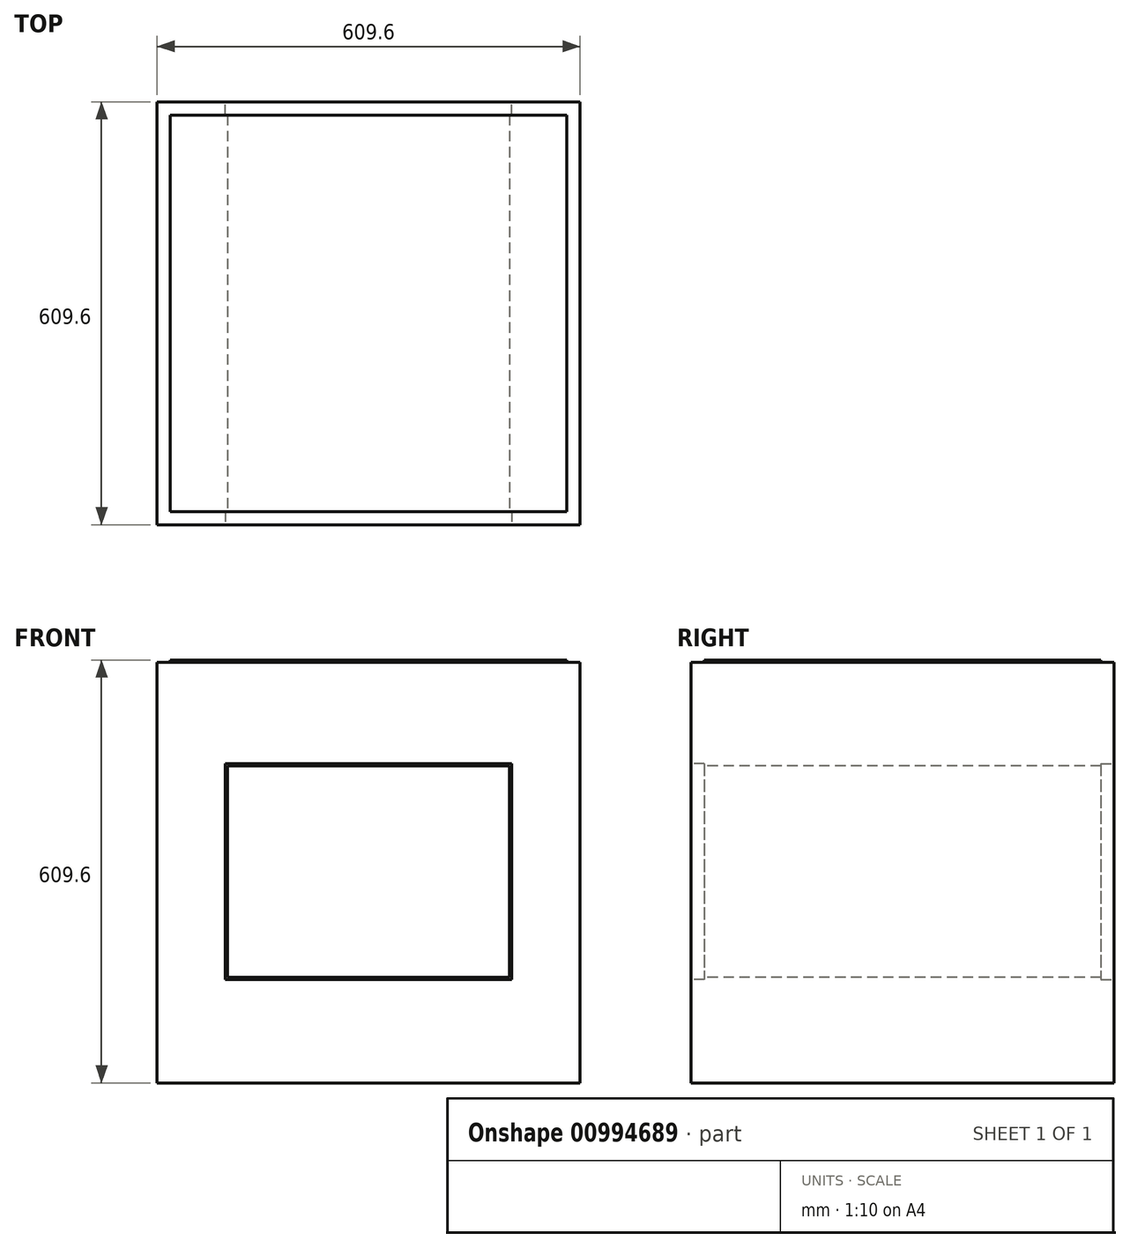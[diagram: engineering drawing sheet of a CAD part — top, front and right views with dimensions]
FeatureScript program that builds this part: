
annotation { "Feature Type Name" : "Feature", "Feature Type Description" : "" }
export const myFeature = defineFeature(function(context is Context, id is Id, definition is map)
    precondition{}
    {
        {
            var Q0;
            Q0=qCreatedBy(makeId("Front.planeOp"),FACE);
            var sketch = newSketch(context, id + "F0", { "sketchPlane" : qUnion([Q0])});
            skLineSegment(sketch, "E0.bottom", {"start": v(0, 0) * mm, "end": v(-609.6, 0) * mm});
            skLineSegment(sketch, "E0.top", {"start": v(0, 609.6) * mm, "end": v(-609.6, 609.6) * mm});
            skLineSegment(sketch, "E0.left", {"start": v(0, 0) * mm, "end": v(0, 609.6) * mm});
            skLineSegment(sketch, "E0.right", {"start": v(-609.6, 0) * mm, "end": v(-609.6, 609.6) * mm});
            skLineSegment(sketch, "E1.bottom", {"start": v(-508, 457.2) * mm, "end": v(-101.6, 457.2) * mm});
            skLineSegment(sketch, "E1.top", {"start": v(-508, 152.4) * mm, "end": v(-101.6, 152.4) * mm});
            skLineSegment(sketch, "E1.left", {"start": v(-508, 457.2) * mm, "end": v(-508, 152.4) * mm});
            skLineSegment(sketch, "E1.right", {"start": v(-101.6, 457.2) * mm, "end": v(-101.6, 152.4) * mm});
            skSolve(sketch);
        }
        {
            var Q0;
            Q0 = qSketchRegion(id + "F0", true);
            extrude(context, id + "F1", {"entities" : qUnion([Q0]), "oppositeDirection" : true, "depth" : 609.6 * mm, "offsetDistance" : 25.4 * mm});
        }
        {
            var Q0;
            Q0=makeQuery(id+"F1.opExtrude","SWEPT_FACE",FACE,{"disambiguationData":[OSD([sQuery(id+"F0.wireOp",EDGE,"E0.top")])]});
            var sketch = newSketch(context, id + "F2", { "sketchPlane" : qUnion([Q0])});
            skLineSegment(sketch, "E2.0", {"start": v(-590.55, 19.05) * mm, "end": v(-19.05, 19.05) * mm});
            skLineSegment(sketch, "E2.1", {"start": v(-590.55, 590.55) * mm, "end": v(-590.55, 19.05) * mm});
            skLineSegment(sketch, "E2.2", {"start": v(-19.05, 590.55) * mm, "end": v(-590.55, 590.55) * mm});
            skLineSegment(sketch, "E2.3", {"start": v(-19.05, 19.05) * mm, "end": v(-19.05, 590.55) * mm});
            skLineSegment(sketch, "E3.bottom", {"start": v(-609.6, 0) * mm, "end": v(0, 0) * mm});
            skLineSegment(sketch, "E3.top", {"start": v(-609.6, 609.6) * mm, "end": v(0, 609.6) * mm});
            skLineSegment(sketch, "E3.left", {"start": v(-609.6, 0) * mm, "end": v(-609.6, 609.6) * mm});
            skLineSegment(sketch, "E3.right", {"start": v(0, 0) * mm, "end": v(0, 609.6) * mm});
            skSolve(sketch);
        }
        {
            var Q0;
            Q0 = qSketchRegion(id + "F2", true);
            extrude(context, id + "F3", {"entities" : qUnion([Q0]), "operationType" : NewBodyOperationType.REMOVE, "oppositeDirection" : true, "depth" : 3.17 * mm, "offsetDistance" : 25.4 * mm});
        }
        {
            var Q0;
            Q0=makeQuery(id+"F1.opExtrude","CAP_FACE",FACE,{"disambiguationData":[OSD([sQuery(id+"F0.wireOp",EDGE,"E0.bottom"),sQuery(id+"F0.wireOp",EDGE,"E0.top"),sQuery(id+"F0.wireOp",EDGE,"E0.left"),sQuery(id+"F0.wireOp",EDGE,"E0.right"),sQuery(id+"F0.wireOp",EDGE,"E1.bottom"),sQuery(id+"F0.wireOp",EDGE,"E1.top"),sQuery(id+"F0.wireOp",EDGE,"E1.left"),sQuery(id+"F0.wireOp",EDGE,"E1.right")])],"isStart":true});
            var sketch = newSketch(context, id + "F4", { "sketchPlane" : qUnion([Q0])});
            skLineSegment(sketch, "E4.bottom", {"start": v(-511.18, 460.37) * mm, "end": v(-98.43, 460.37) * mm});
            skLineSegment(sketch, "E4.top", {"start": v(-511.18, 149.22) * mm, "end": v(-98.43, 149.22) * mm});
            skLineSegment(sketch, "E4.left", {"start": v(-511.18, 460.37) * mm, "end": v(-511.18, 149.22) * mm});
            skLineSegment(sketch, "E4.right", {"start": v(-98.43, 460.37) * mm, "end": v(-98.43, 149.22) * mm});
            skLineSegment(sketch, "E5.bottom", {"start": v(-508, 457.2) * mm, "end": v(-101.6, 457.2) * mm});
            skLineSegment(sketch, "E5.top", {"start": v(-508, 152.4) * mm, "end": v(-101.6, 152.4) * mm});
            skLineSegment(sketch, "E5.left", {"start": v(-508, 457.2) * mm, "end": v(-508, 152.4) * mm});
            skLineSegment(sketch, "E5.right", {"start": v(-101.6, 457.2) * mm, "end": v(-101.6, 152.4) * mm});
            skSolve(sketch);
        }
        {
            var Q0;
            Q0 = qSketchRegion(id + "F4", true);
            extrude(context, id + "F5", {"entities" : qUnion([Q0]), "operationType" : NewBodyOperationType.REMOVE, "oppositeDirection" : true, "depth" : 19.05 * mm, "offsetDistance" : 25.4 * mm});
        }
        {
            var Q0;
            Q0=makeQuery(id+"F1.opExtrude","CAP_FACE",FACE,{"disambiguationData":[OSD([sQuery(id+"F0.wireOp",EDGE,"E0.bottom"),sQuery(id+"F0.wireOp",EDGE,"E0.top"),sQuery(id+"F0.wireOp",EDGE,"E0.left"),sQuery(id+"F0.wireOp",EDGE,"E0.right"),sQuery(id+"F0.wireOp",EDGE,"E1.bottom"),sQuery(id+"F0.wireOp",EDGE,"E1.top"),sQuery(id+"F0.wireOp",EDGE,"E1.left"),sQuery(id+"F0.wireOp",EDGE,"E1.right")])],"isStart":false});
            var sketch = newSketch(context, id + "F6", { "sketchPlane" : qUnion([Q0])});
            skLineSegment(sketch, "E6.bottom", {"start": v(101.6, 457.2) * mm, "end": v(508, 457.2) * mm});
            skLineSegment(sketch, "E6.top", {"start": v(101.6, 152.4) * mm, "end": v(508, 152.4) * mm});
            skLineSegment(sketch, "E6.left", {"start": v(101.6, 457.2) * mm, "end": v(101.6, 152.4) * mm});
            skLineSegment(sketch, "E6.right", {"start": v(508, 457.2) * mm, "end": v(508, 152.4) * mm});
            skLineSegment(sketch, "E7.bottom", {"start": v(98.43, 460.37) * mm, "end": v(511.18, 460.37) * mm});
            skLineSegment(sketch, "E7.top", {"start": v(98.43, 149.22) * mm, "end": v(511.18, 149.22) * mm});
            skLineSegment(sketch, "E7.left", {"start": v(98.43, 460.37) * mm, "end": v(98.43, 149.22) * mm});
            skLineSegment(sketch, "E7.right", {"start": v(511.18, 460.37) * mm, "end": v(511.18, 149.22) * mm});
            skSolve(sketch);
        }
        {
            var Q0;
            Q0 = qSketchRegion(id + "F6", true);
            extrude(context, id + "F7", {"entities" : qUnion([Q0]), "operationType" : NewBodyOperationType.REMOVE, "oppositeDirection" : true, "depth" : 19.05 * mm, "offsetDistance" : 25.4 * mm});
        }
    });
